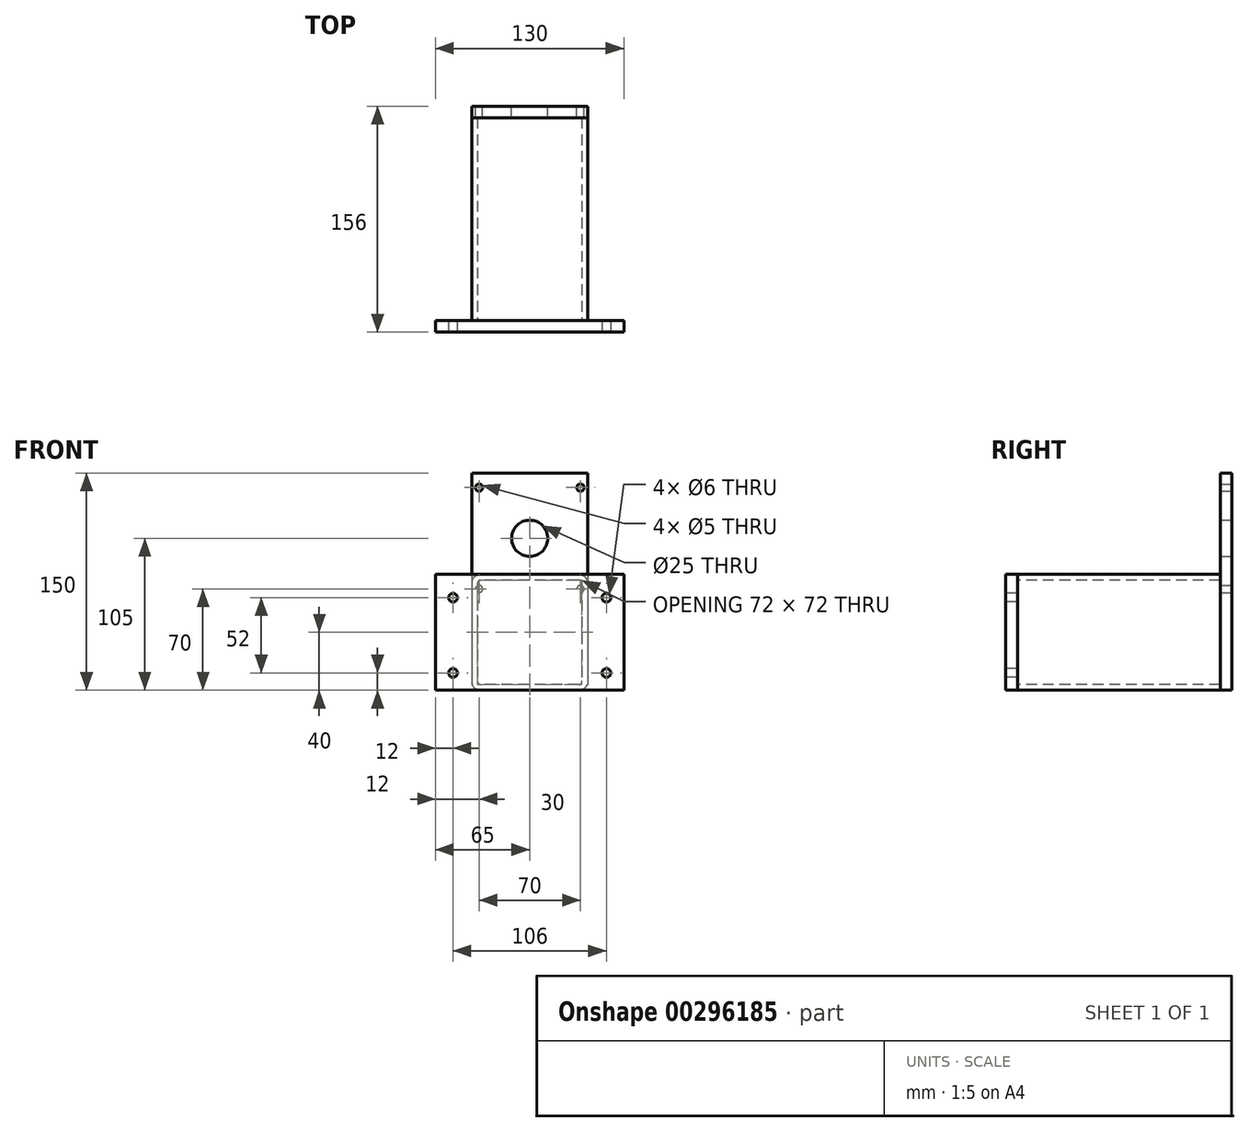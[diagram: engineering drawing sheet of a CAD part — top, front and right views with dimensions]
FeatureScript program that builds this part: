
annotation { "Feature Type Name" : "Feature", "Feature Type Description" : "" }
export const myFeature = defineFeature(function(context is Context, id is Id, definition is map)
    precondition{}
    {
        {
            var Q0;
            Q0=qCreatedBy(makeId("Front.planeOp"),FACE);
            var sketch = newSketch(context, id + "F0", { "sketchPlane" : qUnion([Q0])});
            skLineSegment(sketch, "E0.bottom", {"start": v(34, 40) * mm, "end": v(-34, 40) * mm});
            skLineSegment(sketch, "E0.top", {"start": v(34, -40) * mm, "end": v(-34, -40) * mm});
            skLineSegment(sketch, "E0.left", {"start": v(40, 34) * mm, "end": v(40, -34) * mm});
            skLineSegment(sketch, "E0.right", {"start": v(-40, 34) * mm, "end": v(-40, -34) * mm});
            skPoint(sketch, "E0.middle", {"position": v(0, 0) * mm});
            skPoint(sketch, "E1.visualSharp", {"position": v(-40, 40) * mm});
            skArc(sketch, "E1.filletArc", {"start": v(-34, 40) * mm, "mid": v(-38.24, 38.24) * mm, "end": v(-40, 34) * mm});
            skPoint(sketch, "E2.visualSharp", {"position": v(40, 40) * mm});
            skArc(sketch, "E2.filletArc", {"start": v(40, 34) * mm, "mid": v(38.24, 38.24) * mm, "end": v(34, 40) * mm});
            skPoint(sketch, "E3.visualSharp", {"position": v(40, -40) * mm});
            skArc(sketch, "E3.filletArc", {"start": v(34, -40) * mm, "mid": v(38.24, -38.24) * mm, "end": v(40, -34) * mm});
            skPoint(sketch, "E4.visualSharp", {"position": v(-40, -40) * mm});
            skArc(sketch, "E4.filletArc", {"start": v(-40, -34) * mm, "mid": v(-38.24, -38.24) * mm, "end": v(-34, -40) * mm});
            skArc(sketch, "E5.0", {"start": v(-34, 36) * mm, "mid": v(-35.41, 35.41) * mm, "end": v(-36, 34) * mm});
            skLineSegment(sketch, "E5.1", {"start": v(34, 36) * mm, "end": v(-34, 36) * mm});
            skLineSegment(sketch, "E5.2", {"start": v(-36, 34) * mm, "end": v(-36, -34) * mm});
            skArc(sketch, "E5.3", {"start": v(36, 34) * mm, "mid": v(35.41, 35.41) * mm, "end": v(34, 36) * mm});
            skArc(sketch, "E5.4", {"start": v(-36, -34) * mm, "mid": v(-35.41, -35.41) * mm, "end": v(-34, -36) * mm});
            skLineSegment(sketch, "E5.5", {"start": v(34, -36) * mm, "end": v(-34, -36) * mm});
            skArc(sketch, "E5.6", {"start": v(34, -36) * mm, "mid": v(35.41, -35.41) * mm, "end": v(36, -34) * mm});
            skLineSegment(sketch, "E5.7", {"start": v(36, 34) * mm, "end": v(36, -34) * mm});
            skSolve(sketch);
        }
        {
            var Q0;
            Q0=makeQuery(id+"F0.imprint","IMPRINT",FACE,{"disambiguationData":[TD([[makeQuery(id+"F0.imprint","IMPRINT",EDGE,{"derivedFrom":sQuery(id+"F0.wireOp",EDGE,"E0.bottom")}),1.0]])]});
            extrude(context, id + "F1", {"entities" : qUnion([Q0]), "oppositeDirection" : true, "depth" : (150 - 2 * 8 + 6) * mm, "offsetDistance" : 25 * mm});
        }
        {
            var Q0;
            Q0=qCreatedBy(makeId("Front.planeOp"),FACE);
            cPlane(context, id + "F2", {"entities" : qUnion([Q0]), "cplaneType" : CPlaneType.OFFSET, "offset" : 8 * mm, "width" : 150 * mm, "height" : 150 * mm});
        }
        {
            var Q0;
            Q0=qCreatedBy(id+"F2.planeOp",FACE);
            var sketch = newSketch(context, id + "F3", { "sketchPlane" : qUnion([Q0])});
            skLineSegment(sketch, "E6.bottom", {"start": v(-65, 40) * mm, "end": v(65, 40) * mm});
            skLineSegment(sketch, "E6.top", {"start": v(-65, -40) * mm, "end": v(65, -40) * mm});
            skLineSegment(sketch, "E6.left", {"start": v(-65, 40) * mm, "end": v(-65, -40) * mm});
            skLineSegment(sketch, "E6.right", {"start": v(65, 40) * mm, "end": v(65, -40) * mm});
            skPoint(sketch, "E6.middle", {"position": v(0, 0) * mm});
            skCircle(sketch, "E7", {"center": v(-53, 24) * mm, "radius": 3 * mm});
            skCircle(sketch, "E8", {"center": v(-53, -28) * mm, "radius": 3 * mm});
            skCircle(sketch, "E9", {"center": v(53, -28) * mm, "radius": 3 * mm});
            skCircle(sketch, "E10", {"center": v(53, 24) * mm, "radius": 3 * mm});
            skSolve(sketch);
        }
        {
            var Q0;
            Q0=makeQuery(id+"F3.imprint","IMPRINT",FACE,{"disambiguationData":[TD([[makeQuery(id+"F3.imprint","IMPRINT",EDGE,{"derivedFrom":sQuery(id+"F3.wireOp",EDGE,"E6.bottom")}),-1.0]])]});
            extrude(context, id + "F4", {"entities" : qUnion([Q0]), "oppositeDirection" : true, "depth" : 8 * mm, "offsetDistance" : 25 * mm});
        }
        {
            var Q0;
            Q0=makeQuery(id+"F1.opExtrude","CAP_FACE",FACE,{"disambiguationData":[OSD([sQuery(id+"F0.wireOp",EDGE,"E0.bottom"),sQuery(id+"F0.wireOp",EDGE,"E0.top"),sQuery(id+"F0.wireOp",EDGE,"E0.left"),sQuery(id+"F0.wireOp",EDGE,"E0.right"),sQuery(id+"F0.wireOp",EDGE,"E1.filletArc"),sQuery(id+"F0.wireOp",EDGE,"E2.filletArc"),sQuery(id+"F0.wireOp",EDGE,"E3.filletArc"),sQuery(id+"F0.wireOp",EDGE,"E4.filletArc"),sQuery(id+"F0.wireOp",EDGE,"E5.0"),sQuery(id+"F0.wireOp",EDGE,"E5.1"),sQuery(id+"F0.wireOp",EDGE,"E5.2"),sQuery(id+"F0.wireOp",EDGE,"E5.3"),sQuery(id+"F0.wireOp",EDGE,"E5.4"),sQuery(id+"F0.wireOp",EDGE,"E5.5"),sQuery(id+"F0.wireOp",EDGE,"E5.6"),sQuery(id+"F0.wireOp",EDGE,"E5.7")])],"isStart":false});
            cPlane(context, id + "F5", {"entities" : qUnion([Q0]), "cplaneType" : CPlaneType.OFFSET, "offset" : 8 * mm, "width" : 150 * mm, "height" : 150 * mm});
        }
        {
            var Q0;
            Q0=qCreatedBy(id+"F5.planeOp",FACE);
            var sketch = newSketch(context, id + "F6", { "sketchPlane" : qUnion([Q0])});
            skLineSegment(sketch, "E11.bottom", {"start": v(40, 110) * mm, "end": v(-40, 110) * mm});
            skLineSegment(sketch, "E11.top", {"start": v(40, -40) * mm, "end": v(-40, -40) * mm});
            skLineSegment(sketch, "E11.left", {"start": v(40, 110) * mm, "end": v(40, -40) * mm});
            skLineSegment(sketch, "E11.right", {"start": v(-40, 110) * mm, "end": v(-40, -40) * mm});
            skCircle(sketch, "E12", {"center": v(0, 65) * mm, "radius": 12.5 * mm});
            skLineSegment(sketch, "E13.bottom", {"start": v(35, 100) * mm, "end": v(-35, 100) * mm, "construction": true});
            skLineSegment(sketch, "E13.top", {"start": v(35, 30) * mm, "end": v(-35, 30) * mm, "construction": true});
            skLineSegment(sketch, "E13.left", {"start": v(35, 100) * mm, "end": v(35, 30) * mm, "construction": true});
            skLineSegment(sketch, "E13.right", {"start": v(-35, 100) * mm, "end": v(-35, 30) * mm, "construction": true});
            skCircle(sketch, "E14", {"center": v(35, 100) * mm, "radius": 2.5 * mm});
            skCircle(sketch, "E15", {"center": v(-35, 100) * mm, "radius": 2.5 * mm});
            skCircle(sketch, "E16", {"center": v(-35, 30) * mm, "radius": 2.5 * mm});
            skCircle(sketch, "E17", {"center": v(35, 30) * mm, "radius": 2.5 * mm});
            skSolve(sketch);
        }
        {
            var Q0;
            Q0=makeQuery(id+"F6.imprint","IMPRINT",FACE,{"disambiguationData":[TD([[makeQuery(id+"F6.imprint","IMPRINT",EDGE,{"derivedFrom":sQuery(id+"F6.wireOp",EDGE,"E11.bottom")}),1.0]])]});
            extrude(context, id + "F7", {"entities" : qUnion([Q0]), "oppositeDirection" : true, "depth" : 8 * mm, "offsetDistance" : 25 * mm});
        }
    });
